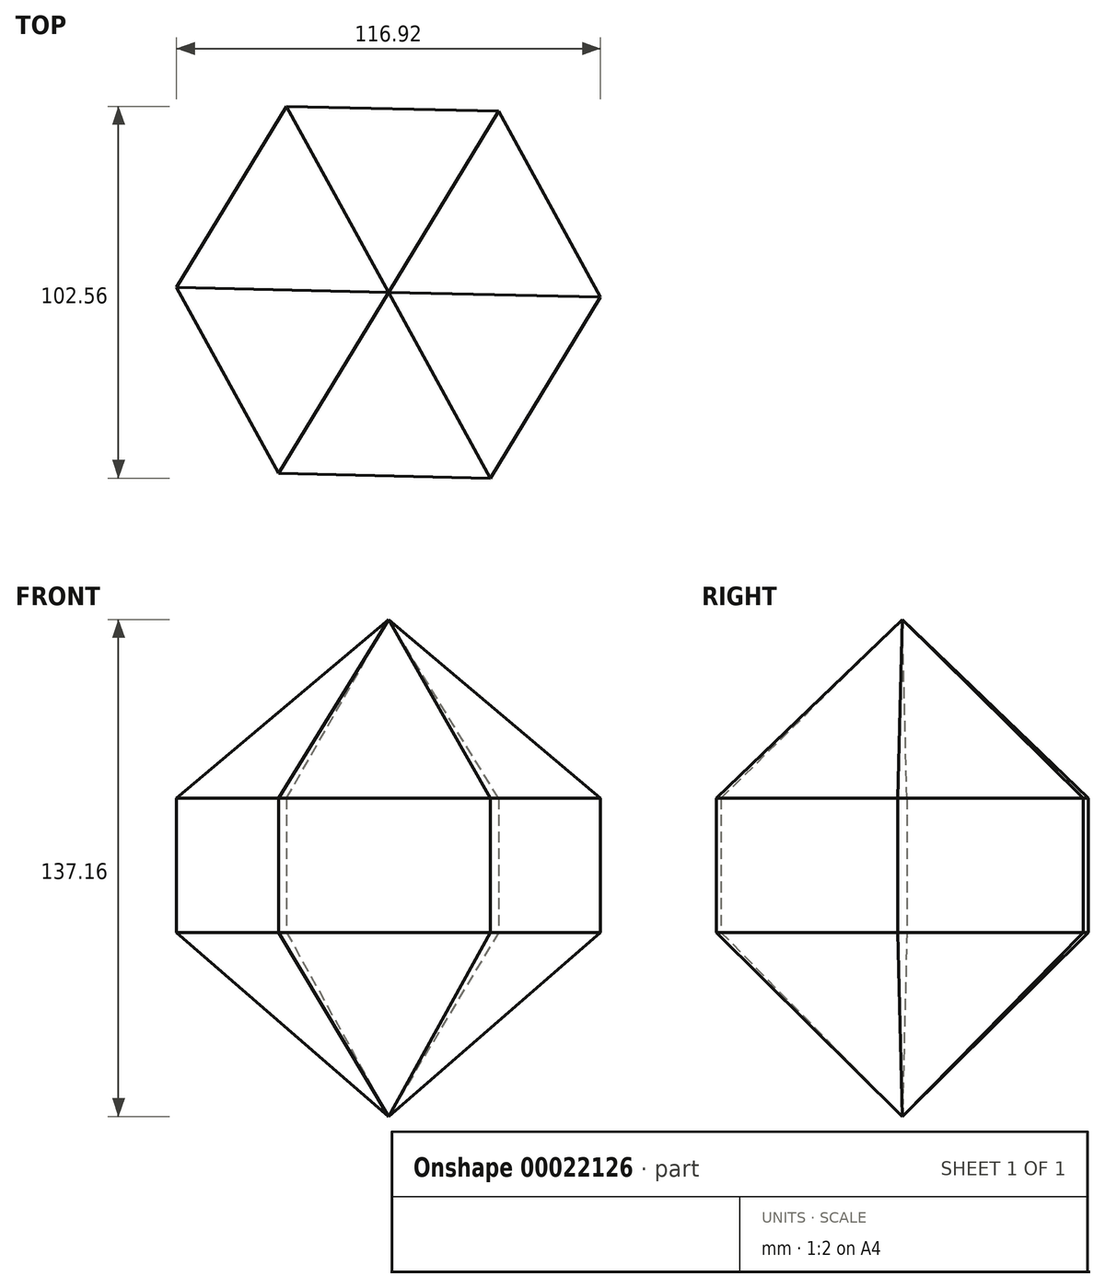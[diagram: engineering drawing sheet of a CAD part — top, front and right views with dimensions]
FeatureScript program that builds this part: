
annotation { "Feature Type Name" : "Feature", "Feature Type Description" : "" }
export const myFeature = defineFeature(function(context is Context, id is Id, definition is map)
    precondition{}
    {
        {
            var Q0;
            Q0=qCreatedBy(makeId("Top.planeOp"),FACE);
            var sketch = newSketch(context, id + "F0", { "sketchPlane" : qUnion([Q0])});
            skCircle(sketch, "E0.cCircle", {"center": v(0, 0) * mm, "radius": 50.64 * mm, "construction": true});
            skLineSegment(sketch, "E0.0", {"start": v(-58.46, 1.3) * mm, "end": v(-28.1, 51.28) * mm});
            skLineSegment(sketch, "E0.1", {"start": v(-28.1, 51.28) * mm, "end": v(30.36, 49.98) * mm});
            skLineSegment(sketch, "E0.2", {"start": v(30.36, 49.98) * mm, "end": v(58.46, -1.3) * mm});
            skLineSegment(sketch, "E0.3", {"start": v(58.46, -1.3) * mm, "end": v(28.1, -51.28) * mm});
            skLineSegment(sketch, "E0.4", {"start": v(28.1, -51.28) * mm, "end": v(-30.36, -49.98) * mm});
            skLineSegment(sketch, "E0.5", {"start": v(-30.36, -49.98) * mm, "end": v(-58.46, 1.3) * mm});
            skPoint(sketch, "E0.0.midPoint", {"position": v(-43.28, 26.29) * mm});
            skSolve(sketch);
        }
        {
            var Q0;
            Q0=makeQuery(id+"F0.imprint","IMPRINT",FACE,{"disambiguationData":[TD([[makeQuery(id+"F0.imprint","IMPRINT",EDGE,{"derivedFrom":sQuery(id+"F0.wireOp",EDGE,"E0.0")}),-1.0]])]});
            extrude(context, id + "F1", {"entities" : qUnion([Q0]), "depth" : 37.02 * mm});
        }
        {
            var Q0;
            Q0=qCreatedBy(makeId("Top.planeOp"),FACE);
            cPlane(context, id + "F2", {"entities" : qUnion([Q0]), "cplaneType" : CPlaneType.OFFSET, "offset" : 86.36 * mm, "width" : 152.4 * mm, "height" : 152.4 * mm});
        }
        {
            var Q0;
            Q0=qCreatedBy(id+"F2.planeOp",FACE);
            var sketch = newSketch(context, id + "F3", { "sketchPlane" : qUnion([Q0])});
            skPoint(sketch, "E1", {"position": v(0, 0) * mm});
            skSolve(sketch);
        }
        {
            var Q1;
            Q1=makeQuery(id+"F1.opExtrude","CAP_FACE",FACE,{"disambiguationData":[OSD([sQuery(id+"F0.wireOp",EDGE,"E0.0"),sQuery(id+"F0.wireOp",EDGE,"E0.1"),sQuery(id+"F0.wireOp",EDGE,"E0.2"),sQuery(id+"F0.wireOp",EDGE,"E0.3"),sQuery(id+"F0.wireOp",EDGE,"E0.4"),sQuery(id+"F0.wireOp",EDGE,"E0.5")])],"isStart":false});
            var Q2;
            Q2=sQuery(id+"F3.wireOp",VERTEX,"E1");
            loft(context, id + "F4", {"operationType" : NewBodyOperationType.ADD, "sheetProfilesArray" : [{ "sheetProfileEntities" : qUnion([Q1]) }, { "sheetProfileEntities" : qUnion([Q2]) }]});
        }
        {
            var Q0;
            Q0=qCreatedBy(makeId("Top.planeOp"),FACE);
            cPlane(context, id + "F5", {"entities" : qUnion([Q0]), "cplaneType" : CPlaneType.OFFSET, "offset" : 50.8 * mm, "oppositeDirection" : true, "width" : 152.4 * mm, "height" : 152.4 * mm});
        }
        {
            var Q0;
            Q0=qCreatedBy(id+"F5.planeOp",FACE);
            var sketch = newSketch(context, id + "F6", { "sketchPlane" : qUnion([Q0])});
            skPoint(sketch, "E2", {"position": v(0, 0) * mm});
            skSolve(sketch);
        }
        {
            var Q1;
            Q1=makeQuery(id+"F1.opExtrude","CAP_FACE",FACE,{"disambiguationData":[OSD([sQuery(id+"F0.wireOp",EDGE,"E0.0"),sQuery(id+"F0.wireOp",EDGE,"E0.1"),sQuery(id+"F0.wireOp",EDGE,"E0.2"),sQuery(id+"F0.wireOp",EDGE,"E0.3"),sQuery(id+"F0.wireOp",EDGE,"E0.4"),sQuery(id+"F0.wireOp",EDGE,"E0.5")])],"isStart":true});
            var Q2;
            Q2=sQuery(id+"F6.wireOp",VERTEX,"E2");
            loft(context, id + "F7", {"operationType" : NewBodyOperationType.ADD, "sheetProfilesArray" : [{ "sheetProfileEntities" : qUnion([Q1]) }, { "sheetProfileEntities" : qUnion([Q2]) }]});
        }
    });
